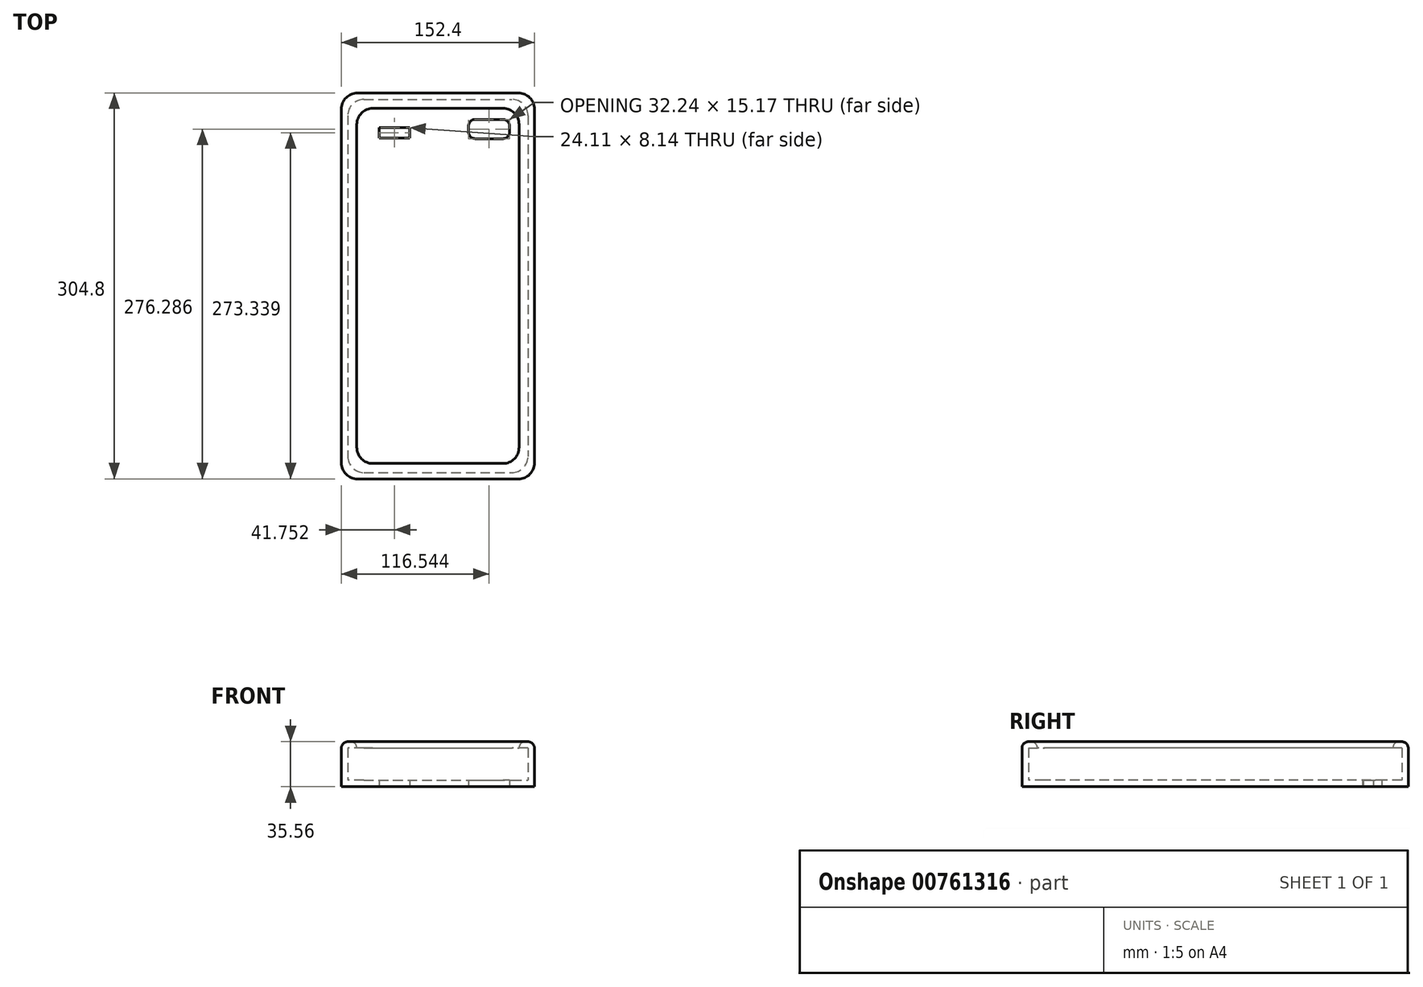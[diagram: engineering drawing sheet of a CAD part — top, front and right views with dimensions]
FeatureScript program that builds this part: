
annotation { "Feature Type Name" : "Feature", "Feature Type Description" : "" }
export const myFeature = defineFeature(function(context is Context, id is Id, definition is map)
    precondition{}
    {
        {
            var Q0;
            Q0=qCreatedBy(makeId("Top.planeOp"),FACE);
            var sketch = newSketch(context, id + "F0", { "sketchPlane" : qUnion([Q0])});
            skLineSegment(sketch, "E0.bottom", {"start": v(-152.4, 304.8) * mm, "end": v(0, 304.8) * mm});
            skLineSegment(sketch, "E0.top", {"start": v(-152.4, 0) * mm, "end": v(0, 0) * mm});
            skLineSegment(sketch, "E0.left", {"start": v(-152.4, 304.8) * mm, "end": v(-152.4, 0) * mm});
            skLineSegment(sketch, "E0.right", {"start": v(0, 304.8) * mm, "end": v(0, 0) * mm});
            skSolve(sketch);
        }
        {
            var Q0;
            Q0=makeQuery(id+"F0.imprint","IMPRINT",FACE,{"disambiguationData":[TD([[makeQuery(id+"F0.imprint","IMPRINT",EDGE,{"derivedFrom":sQuery(id+"F0.wireOp",EDGE,"E0.bottom")}),-1.0]])]});
            extrude(context, id + "F1", {"entities" : qUnion([Q0]), "depth" : 5.08 * mm, "offsetDistance" : 25.4 * mm});
        }
        {
            var Q0;
            Q0=makeQuery(id+"F1.opExtrude","CAP_FACE",FACE,{"disambiguationData":[OSD([sQuery(id+"F0.wireOp",EDGE,"E0.bottom"),sQuery(id+"F0.wireOp",EDGE,"E0.top"),sQuery(id+"F0.wireOp",EDGE,"E0.left"),sQuery(id+"F0.wireOp",EDGE,"E0.right")])],"isStart":false});
            var sketch = newSketch(context, id + "F2", { "sketchPlane" : qUnion([Q0])});
            skLineSegment(sketch, "E1.bottom", {"start": v(-152.4, 304.8) * mm, "end": v(0, 304.8) * mm});
            skLineSegment(sketch, "E1.top", {"start": v(-152.4, 0) * mm, "end": v(0, 0) * mm});
            skLineSegment(sketch, "E1.left", {"start": v(-152.4, 304.8) * mm, "end": v(-152.4, 0) * mm});
            skLineSegment(sketch, "E1.right", {"start": v(0, 304.8) * mm, "end": v(0, 0) * mm});
            skLineSegment(sketch, "E2.0", {"start": v(-147.32, 299.72) * mm, "end": v(-5.08, 299.72) * mm});
            skLineSegment(sketch, "E2.1", {"start": v(-147.32, 299.72) * mm, "end": v(-147.32, 5.08) * mm});
            skLineSegment(sketch, "E2.2", {"start": v(-147.32, 5.08) * mm, "end": v(-5.08, 5.08) * mm});
            skLineSegment(sketch, "E2.3", {"start": v(-5.08, 299.72) * mm, "end": v(-5.08, 5.08) * mm});
            skSolve(sketch);
        }
        {
            var Q0;
            Q0=makeQuery(id+"F2.imprint","IMPRINT",FACE,{"disambiguationData":[TD([[makeQuery(id+"F2.imprint","IMPRINT",EDGE,{"derivedFrom":sQuery(id+"F2.wireOp",EDGE,"E1.bottom")}),-1.0]])]});
            extrude(context, id + "F3", {"entities" : qUnion([Q0]), "operationType" : NewBodyOperationType.ADD, "depth" : 25.4 * mm, "offsetDistance" : 25.4 * mm});
        }
        {
            var Q0;
            Q0=makeQuery(id+"F3.opExtrude","CAP_FACE",FACE,{"disambiguationData":[OSD([sQuery(id+"F2.wireOp",EDGE,"E1.bottom"),sQuery(id+"F2.wireOp",EDGE,"E1.top"),sQuery(id+"F2.wireOp",EDGE,"E1.left"),sQuery(id+"F2.wireOp",EDGE,"E1.right"),sQuery(id+"F2.wireOp",EDGE,"E2.0"),sQuery(id+"F2.wireOp",EDGE,"E2.1"),sQuery(id+"F2.wireOp",EDGE,"E2.2"),sQuery(id+"F2.wireOp",EDGE,"E2.3")])],"isStart":false});
            var sketch = newSketch(context, id + "F4", { "sketchPlane" : qUnion([Q0])});
            skLineSegment(sketch, "E3.bottom", {"start": v(-152.4, 304.8) * mm, "end": v(0, 304.8) * mm});
            skLineSegment(sketch, "E3.top", {"start": v(-152.4, 0) * mm, "end": v(0, 0) * mm});
            skLineSegment(sketch, "E3.left", {"start": v(-152.4, 304.8) * mm, "end": v(-152.4, 0) * mm});
            skLineSegment(sketch, "E3.right", {"start": v(0, 304.8) * mm, "end": v(0, 0) * mm});
            skLineSegment(sketch, "E4.0", {"start": v(-12.2, 292.6) * mm, "end": v(-12.2, 12.2) * mm});
            skLineSegment(sketch, "E4.1", {"start": v(-140.2, 292.6) * mm, "end": v(-12.2, 292.6) * mm});
            skLineSegment(sketch, "E4.2", {"start": v(-140.2, 292.6) * mm, "end": v(-140.2, 12.2) * mm});
            skLineSegment(sketch, "E4.3", {"start": v(-140.2, 12.2) * mm, "end": v(-12.2, 12.2) * mm});
            skSolve(sketch);
        }
        {
            var Q0;
            Q0=makeQuery(id+"F4.imprint","IMPRINT",FACE,{"disambiguationData":[TD([[makeQuery(id+"F4.imprint","IMPRINT",EDGE,{"derivedFrom":sQuery(id+"F4.wireOp",EDGE,"E3.bottom")}),-1.0]])]});
            var Q1;
            Q1=makeQuery(id+"F4.imprint","IMPRINT",FACE,{"disambiguationData":[TD([[makeQuery(id+"F4.imprint","IMPRINT",EDGE,{"derivedFrom":sQuery(id+"F4.wireOp",EDGE,"E4.0")}),1.0]])]});
            extrude(context, id + "F5", {"entities" : qUnion([Q0, Q1]), "operationType" : NewBodyOperationType.ADD, "depth" : 5.08 * mm, "offsetDistance" : 25.4 * mm});
        }
        {
            var Q0;
            Q0=makeQuery(id+"F5.boolean.opBoolean","MERGE",EDGE,{"derivedFrom":[makeQuery(id+"F3.boolean.opBoolean","MERGE",EDGE,{"derivedFrom":[makeQuery(id+"F1.opExtrude","SWEPT_EDGE",EDGE,{"disambiguationData":[OSD([sQuery(id+"F0.wireOp",EDGE,"E0.top"),sQuery(id+"F0.wireOp",EDGE,"E0.left")])]}),makeQuery(id+"F3.opExtrude","SWEPT_EDGE",EDGE,{"disambiguationData":[OSD([sQuery(id+"F2.wireOp",EDGE,"E1.top"),sQuery(id+"F2.wireOp",EDGE,"E1.left")])]})]}),makeQuery(id+"F5.opExtrude","SWEPT_EDGE",EDGE,{"disambiguationData":[OSD([sQuery(id+"F4.wireOp",EDGE,"E3.top"),sQuery(id+"F4.wireOp",EDGE,"E3.left")])]})]});
            var Q1;
            Q1=makeQuery(id+"F5.boolean.opBoolean","MERGE",EDGE,{"derivedFrom":[makeQuery(id+"F3.boolean.opBoolean","MERGE",EDGE,{"derivedFrom":[makeQuery(id+"F1.opExtrude","SWEPT_EDGE",EDGE,{"disambiguationData":[OSD([sQuery(id+"F0.wireOp",EDGE,"E0.top"),sQuery(id+"F0.wireOp",EDGE,"E0.right")])]}),makeQuery(id+"F3.opExtrude","SWEPT_EDGE",EDGE,{"disambiguationData":[OSD([sQuery(id+"F2.wireOp",EDGE,"E1.top"),sQuery(id+"F2.wireOp",EDGE,"E1.right")])]})]}),makeQuery(id+"F5.opExtrude","SWEPT_EDGE",EDGE,{"disambiguationData":[OSD([sQuery(id+"F4.wireOp",EDGE,"E3.top"),sQuery(id+"F4.wireOp",EDGE,"E3.right")])]})]});
            var Q2;
            Q2=makeQuery(id+"F5.boolean.opBoolean","MERGE",EDGE,{"derivedFrom":[makeQuery(id+"F3.boolean.opBoolean","MERGE",EDGE,{"derivedFrom":[makeQuery(id+"F1.opExtrude","SWEPT_EDGE",EDGE,{"disambiguationData":[OSD([sQuery(id+"F0.wireOp",EDGE,"E0.bottom"),sQuery(id+"F0.wireOp",EDGE,"E0.right")])]}),makeQuery(id+"F3.opExtrude","SWEPT_EDGE",EDGE,{"disambiguationData":[OSD([sQuery(id+"F2.wireOp",EDGE,"E1.bottom"),sQuery(id+"F2.wireOp",EDGE,"E1.right")])]})]}),makeQuery(id+"F5.opExtrude","SWEPT_EDGE",EDGE,{"disambiguationData":[OSD([sQuery(id+"F4.wireOp",EDGE,"E3.bottom"),sQuery(id+"F4.wireOp",EDGE,"E3.right")])]})]});
            var Q3;
            Q3=makeQuery(id+"F5.boolean.opBoolean","MERGE",EDGE,{"derivedFrom":[makeQuery(id+"F3.boolean.opBoolean","MERGE",EDGE,{"derivedFrom":[makeQuery(id+"F1.opExtrude","SWEPT_EDGE",EDGE,{"disambiguationData":[OSD([sQuery(id+"F0.wireOp",EDGE,"E0.bottom"),sQuery(id+"F0.wireOp",EDGE,"E0.left")])]}),makeQuery(id+"F3.opExtrude","SWEPT_EDGE",EDGE,{"disambiguationData":[OSD([sQuery(id+"F2.wireOp",EDGE,"E1.bottom"),sQuery(id+"F2.wireOp",EDGE,"E1.left")])]})]}),makeQuery(id+"F5.opExtrude","SWEPT_EDGE",EDGE,{"disambiguationData":[OSD([sQuery(id+"F4.wireOp",EDGE,"E3.bottom"),sQuery(id+"F4.wireOp",EDGE,"E3.left")])]})]});
            var Q4;
            Q4=makeQuery(id+"F3.opExtrude","SWEPT_EDGE",EDGE,{"disambiguationData":[OSD([sQuery(id+"F2.wireOp",EDGE,"E2.1"),sQuery(id+"F2.wireOp",EDGE,"E2.2")])]});
            var Q5;
            Q5=makeQuery(id+"F3.opExtrude","SWEPT_EDGE",EDGE,{"disambiguationData":[OSD([sQuery(id+"F2.wireOp",EDGE,"E2.2"),sQuery(id+"F2.wireOp",EDGE,"E2.3")])]});
            var Q6;
            Q6=makeQuery(id+"F3.opExtrude","SWEPT_EDGE",EDGE,{"disambiguationData":[OSD([sQuery(id+"F2.wireOp",EDGE,"E2.0"),sQuery(id+"F2.wireOp",EDGE,"E2.3")])]});
            var Q7;
            Q7=makeQuery(id+"F3.opExtrude","SWEPT_EDGE",EDGE,{"disambiguationData":[OSD([sQuery(id+"F2.wireOp",EDGE,"E2.0"),sQuery(id+"F2.wireOp",EDGE,"E2.1")])]});
            var Q8;
            Q8=makeQuery(id+"F5.opExtrude","SWEPT_EDGE",EDGE,{"disambiguationData":[OSD([sQuery(id+"F4.wireOp",EDGE,"E4.2"),sQuery(id+"F4.wireOp",EDGE,"E4.3")])]});
            var Q9;
            Q9=makeQuery(id+"F5.opExtrude","SWEPT_EDGE",EDGE,{"disambiguationData":[OSD([sQuery(id+"F4.wireOp",EDGE,"E4.0"),sQuery(id+"F4.wireOp",EDGE,"E4.1")])]});
            var Q10;
            Q10=makeQuery(id+"F5.opExtrude","SWEPT_EDGE",EDGE,{"disambiguationData":[OSD([sQuery(id+"F4.wireOp",EDGE,"E4.1"),sQuery(id+"F4.wireOp",EDGE,"E4.2")])]});
            var Q11;
            Q11=makeQuery(id+"F5.opExtrude","SWEPT_EDGE",EDGE,{"disambiguationData":[OSD([sQuery(id+"F4.wireOp",EDGE,"E4.0"),sQuery(id+"F4.wireOp",EDGE,"E4.3")])]});
            fillet(context, id + "F6", {"entities" : qUnion([Q0, Q1, Q2, Q3, Q4, Q5, Q6, Q7, Q8, Q9, Q10, Q11]), "radius" : 12.7 * mm, "tangentPropagation" : true, "allowEdgeOverflow" : false});
        }
        {
            var Q0;
            Q0=makeQuery(id+"F1.opExtrude","CAP_FACE",FACE,{"disambiguationData":[OSD([sQuery(id+"F0.wireOp",EDGE,"E0.bottom"),sQuery(id+"F0.wireOp",EDGE,"E0.top"),sQuery(id+"F0.wireOp",EDGE,"E0.left"),sQuery(id+"F0.wireOp",EDGE,"E0.right")])],"isStart":true});
            var sketch = newSketch(context, id + "F7", { "sketchPlane" : qUnion([Q0])});
            skLineSegment(sketch, "E5.bottom", {"start": v(-19.74, -283.87) * mm, "end": v(-51.98, -283.87) * mm});
            skLineSegment(sketch, "E5.top", {"start": v(-19.74, -268.7) * mm, "end": v(-51.98, -268.7) * mm});
            skLineSegment(sketch, "E5.left", {"start": v(-19.74, -283.87) * mm, "end": v(-19.74, -268.7) * mm});
            skLineSegment(sketch, "E5.right", {"start": v(-51.98, -283.87) * mm, "end": v(-51.98, -268.7) * mm});
            skSolve(sketch);
        }
        {
            var Q0;
            Q0 = qSketchRegion(id + "F7", true);
            extrude(context, id + "F8", {"entities" : qUnion([Q0]), "operationType" : NewBodyOperationType.REMOVE, "oppositeDirection" : true, "depth" : 25.4 * mm, "offsetDistance" : 25.4 * mm});
        }
        {
            var Q0;
            Q0=makeQuery(id+"F8.boolean.opBoolean","COPY",EDGE,{"derivedFrom":makeQuery(id+"F8.opExtrude","SWEPT_EDGE",EDGE,{"disambiguationData":[OSD([sQuery(id+"F7.wireOp",EDGE,"E5.bottom"),sQuery(id+"F7.wireOp",EDGE,"E5.right")])]})});
            var Q1;
            Q1=makeQuery(id+"F8.boolean.opBoolean","COPY",EDGE,{"derivedFrom":makeQuery(id+"F8.opExtrude","SWEPT_EDGE",EDGE,{"disambiguationData":[OSD([sQuery(id+"F7.wireOp",EDGE,"E5.bottom"),sQuery(id+"F7.wireOp",EDGE,"E5.left")])]})});
            var Q2;
            Q2=makeQuery(id+"F8.boolean.opBoolean","COPY",EDGE,{"derivedFrom":makeQuery(id+"F8.opExtrude","SWEPT_EDGE",EDGE,{"disambiguationData":[OSD([sQuery(id+"F7.wireOp",EDGE,"E5.top"),sQuery(id+"F7.wireOp",EDGE,"E5.left")])]})});
            var Q3;
            Q3=makeQuery(id+"F8.boolean.opBoolean","COPY",EDGE,{"derivedFrom":makeQuery(id+"F8.opExtrude","SWEPT_EDGE",EDGE,{"disambiguationData":[OSD([sQuery(id+"F7.wireOp",EDGE,"E5.top"),sQuery(id+"F7.wireOp",EDGE,"E5.right")])]})});
            var Q4;
            Q4=makeQuery(id+"F5.opExtrude","CAP_FACE",FACE,{"disambiguationData":[OSD([sQuery(id+"F4.wireOp",EDGE,"E3.bottom"),sQuery(id+"F4.wireOp",EDGE,"E3.top"),sQuery(id+"F4.wireOp",EDGE,"E3.left"),sQuery(id+"F4.wireOp",EDGE,"E3.right"),sQuery(id+"F4.wireOp",EDGE,"E4.0"),sQuery(id+"F4.wireOp",EDGE,"E4.1"),sQuery(id+"F4.wireOp",EDGE,"E4.2"),sQuery(id+"F4.wireOp",EDGE,"E4.3")])],"isStart":false});
            fillet(context, id + "F9", {"entities" : qUnion([Q0, Q1, Q2, Q3, Q4]), "radius" : 5.08 * mm, "tangentPropagation" : true, "allowEdgeOverflow" : false});
        }
        {
            var Q0;
            Q0=makeQuery(id+"F1.opExtrude","CAP_FACE",FACE,{"disambiguationData":[OSD([sQuery(id+"F0.wireOp",EDGE,"E0.bottom"),sQuery(id+"F0.wireOp",EDGE,"E0.top"),sQuery(id+"F0.wireOp",EDGE,"E0.left"),sQuery(id+"F0.wireOp",EDGE,"E0.right")])],"isStart":true});
            var sketch = newSketch(context, id + "F10", { "sketchPlane" : qUnion([Q0])});
            skLineSegment(sketch, "E6.bottom", {"start": v(-98.6, -277.4) * mm, "end": v(-122.7, -277.4) * mm});
            skLineSegment(sketch, "E6.top", {"start": v(-98.6, -269.27) * mm, "end": v(-122.7, -269.27) * mm});
            skLineSegment(sketch, "E6.left", {"start": v(-98.6, -277.4) * mm, "end": v(-98.6, -269.27) * mm});
            skLineSegment(sketch, "E6.right", {"start": v(-122.7, -277.4) * mm, "end": v(-122.7, -269.27) * mm});
            skSolve(sketch);
        }
        {
            var Q0;
            Q0 = qSketchRegion(id + "F10", true);
            extrude(context, id + "F11", {"entities" : qUnion([Q0]), "operationType" : NewBodyOperationType.REMOVE, "oppositeDirection" : true, "depth" : 25.4 * mm, "offsetDistance" : 25.4 * mm});
        }
    });
